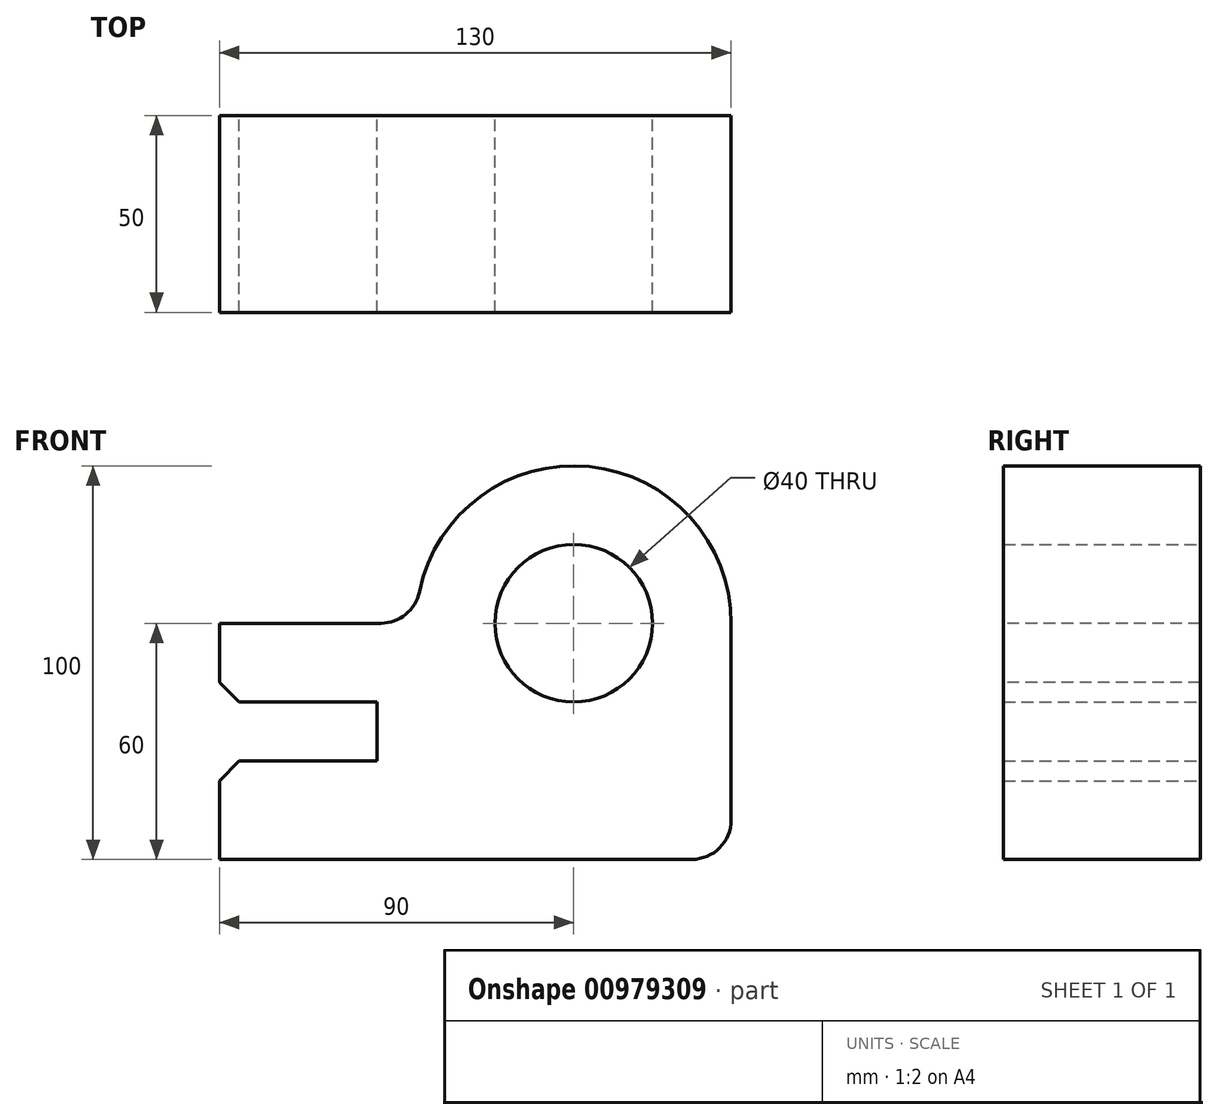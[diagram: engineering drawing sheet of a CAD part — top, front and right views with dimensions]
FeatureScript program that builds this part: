
annotation { "Feature Type Name" : "Feature", "Feature Type Description" : "" }
export const myFeature = defineFeature(function(context is Context, id is Id, definition is map)
    precondition{}
    {
        {
            var Q0;
            Q0=qCreatedBy(makeId("Front.planeOp"),FACE);
            var sketch = newSketch(context, id + "F0", { "sketchPlane" : qUnion([Q0])});
            skLineSegment(sketch, "E0.bottom", {"start": v(0, 0) * mm, "end": v(-130, 0) * mm});
            skLineSegment(sketch, "E0.top", {"start": v(0, 60) * mm, "end": v(-130, 60) * mm});
            skLineSegment(sketch, "E0.left", {"start": v(0, 0) * mm, "end": v(0, 60) * mm});
            skLineSegment(sketch, "E0.right", {"start": v(-130, 0) * mm, "end": v(-130, 60) * mm});
            skArc(sketch, "E1", {"start": v(0, 60) * mm, "mid": v(-40, 100) * mm, "end": v(-80, 60) * mm});
            skCircle(sketch, "E2", {"center": v(-40, 60) * mm, "radius": 20 * mm});
            skLineSegment(sketch, "E3.bottom", {"start": v(-130, 40) * mm, "end": v(-90, 40) * mm});
            skLineSegment(sketch, "E3.top", {"start": v(-130, 25) * mm, "end": v(-90, 25) * mm});
            skLineSegment(sketch, "E3.left", {"start": v(-130, 40) * mm, "end": v(-130, 25) * mm});
            skLineSegment(sketch, "E3.right", {"start": v(-90, 40) * mm, "end": v(-90, 25) * mm});
            skSolve(sketch);
        }
        {
            var Q0;
            {var subQ5=sQuery(id+"F0.wireOp",EDGE,"E0.bottom");Q0=makeQuery(id+"F0.imprint","IMPRINT",FACE,{"disambiguationData":[TD([[makeQuery(id+"F0.imprint","IMPRINT",EDGE,{"derivedFrom":subQ5}),-1.0]])]});}
            var Q1;
            {var subQ0=sQuery(id+"F0.wireOp",EDGE,"E1");Q1=makeQuery(id+"F0.imprint","IMPRINT",FACE,{"disambiguationData":[TD([[makeQuery(id+"F0.imprint","IMPRINT",EDGE,{"derivedFrom":subQ0}),1.0]])]});}
            extrude(context, id + "F1", {"entities" : qUnion([Q0, Q1]), "depth" : 50 * mm, "offsetDistance" : 25 * mm});
        }
        {
            var Q0;
            Q0=makeQuery(id+"F1.opExtrude","SWEPT_EDGE",EDGE,{"disambiguationData":[OSD([sQuery(id+"F0.wireOp",EDGE,"E0.top"),sQuery(id+"F0.wireOp",EDGE,"E1")])]});
            var Q1;
            Q1=makeQuery(id+"F1.opExtrude","SWEPT_EDGE",EDGE,{"disambiguationData":[OSD([sQuery(id+"F0.wireOp",EDGE,"E0.bottom"),sQuery(id+"F0.wireOp",EDGE,"E0.left")])]});
            fillet(context, id + "F2", {"entities" : qUnion([Q0, Q1]), "radius" : 10 * mm, "tangentPropagation" : true, "allowEdgeOverflow" : false});
        }
        {
            var Q0;
            Q0=makeQuery(id+"F1.opExtrude","SWEPT_EDGE",EDGE,{"disambiguationData":[OSD([sQuery(id+"F0.wireOp",EDGE,"E0.right"),sQuery(id+"F0.wireOp",EDGE,"E3.bottom")])]});
            var Q1;
            Q1=makeQuery(id+"F1.opExtrude","SWEPT_EDGE",EDGE,{"disambiguationData":[OSD([sQuery(id+"F0.wireOp",EDGE,"E0.right"),sQuery(id+"F0.wireOp",EDGE,"E3.top")])]});
            chamfer(context, id + "F3", {"entities" : qUnion([Q0, Q1]), "width" : 5 * mm, "tangentPropagation" : true});
        }
    });
